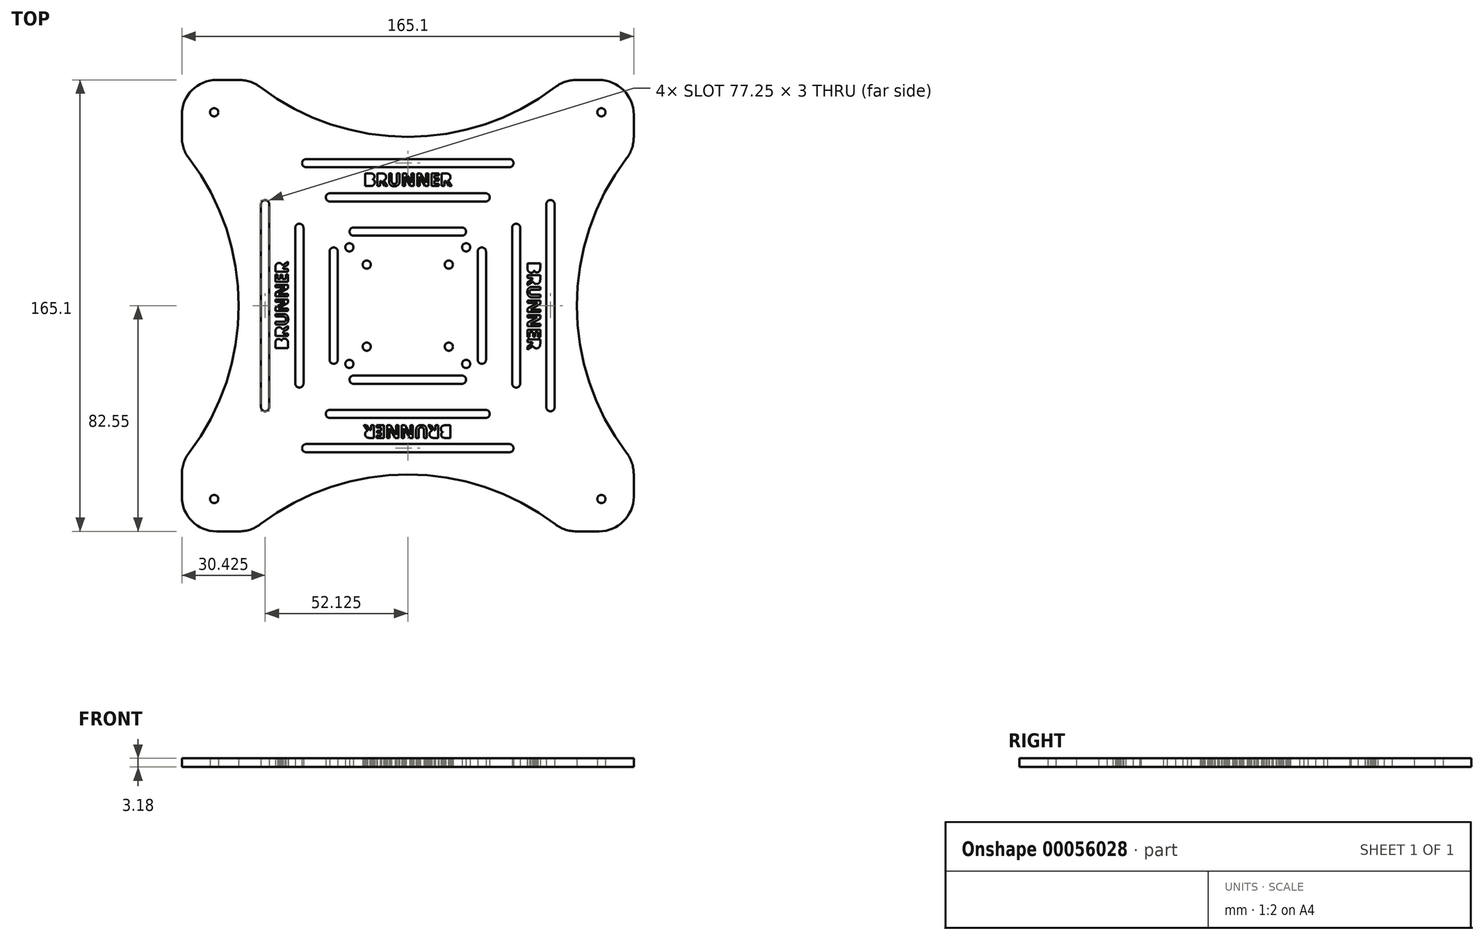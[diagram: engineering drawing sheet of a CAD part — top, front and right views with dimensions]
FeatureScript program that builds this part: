
annotation { "Feature Type Name" : "Feature", "Feature Type Description" : "" }
export const myFeature = defineFeature(function(context is Context, id is Id, definition is map)
    precondition{}
    {
        {
            var Q0;
            Q0=qCreatedBy(makeId("Top.planeOp"),FACE);
            var sketch = newSketch(context, id + "F0", { "sketchPlane" : qUnion([Q0])});
            skLineSegment(sketch, "E0.rect.bottom", {"start": v(-82.55, 82.55) * mm, "end": v(82.55, 82.55) * mm});
            skLineSegment(sketch, "E0.rect.top", {"start": v(-82.55, -82.55) * mm, "end": v(82.55, -82.55) * mm});
            skLineSegment(sketch, "E0.rect.left", {"start": v(-82.55, 82.55) * mm, "end": v(-82.55, -82.55) * mm});
            skLineSegment(sketch, "E0.rect.right", {"start": v(82.55, 82.55) * mm, "end": v(82.55, -82.55) * mm});
            skPoint(sketch, "E0.rect.middle", {"position": v(0, 0) * mm});
            skCircle(sketch, "E1", {"center": v(-70.72, 70.72) * mm, "radius": 1.5 * mm});
            skLineSegment(sketch, "E2", {"start": v(0, 0) * mm, "end": v(-82.55, 82.55) * mm});
            skCircle(sketch, "E3", {"center": v(-15, 15) * mm, "radius": 1.5 * mm});
            skArc(sketch, "E4", {"start": v(-82.55, -57.15) * mm, "mid": v(-61.75, 0) * mm, "end": v(-82.55, 57.15) * mm});
            skArc(sketch, "E5.1.0", {"start": v(-57.15, 82.55) * mm, "mid": v(0, 61.75) * mm, "end": v(57.15, 82.55) * mm});
            skLineSegment(sketch, "E5.anchor1", {"start": v(0, 0) * mm, "end": v(-82.55, -57.15) * mm, "construction": true});
            skLineSegment(sketch, "E5.anchor2", {"start": v(0, 0) * mm, "end": v(-57.15, 82.55) * mm, "construction": true});
            skLineSegment(sketch, "E6", {"start": v(-19.78, 28.58) * mm, "end": v(19.78, 28.58) * mm});
            skLineSegment(sketch, "E7", {"start": v(0, 28.58) * mm, "end": v(0, 82.55) * mm, "construction": true});
            skLineSegment(sketch, "E8.0", {"start": v(-19.78, 25.58) * mm, "end": v(19.78, 25.58) * mm});
            skLineSegment(sketch, "E9.0", {"start": v(-28.45, 38.1) * mm, "end": v(28.45, 38.1) * mm});
            skLineSegment(sketch, "E10.0", {"start": v(-28.45, 41.1) * mm, "end": v(28.45, 41.1) * mm});
            skLineSegment(sketch, "E11.0", {"start": v(-37.13, 50.63) * mm, "end": v(37.13, 50.63) * mm});
            skLineSegment(sketch, "E12.0", {"start": v(-37.13, 53.63) * mm, "end": v(37.13, 53.63) * mm});
            skLineSegment(sketch, "E13", {"start": v(0, 0) * mm, "end": v(57.15, 82.55) * mm, "construction": true});
            skLineSegment(sketch, "E14", {"start": v(-37.13, 53.63) * mm, "end": v(-37.13, 50.63) * mm, "construction": true});
            skLineSegment(sketch, "E15", {"start": v(-28.45, 41.1) * mm, "end": v(-28.45, 38.1) * mm, "construction": true});
            skLineSegment(sketch, "E16", {"start": v(-19.78, 28.58) * mm, "end": v(-19.78, 25.58) * mm, "construction": true});
            skArc(sketch, "E17", {"start": v(-19.78, 28.58) * mm, "mid": v(-21.28, 27.08) * mm, "end": v(-19.78, 25.58) * mm});
            skArc(sketch, "E18", {"start": v(-28.45, 41.1) * mm, "mid": v(-29.95, 39.6) * mm, "end": v(-28.45, 38.1) * mm});
            skArc(sketch, "E19", {"start": v(-37.13, 53.63) * mm, "mid": v(-38.63, 52.13) * mm, "end": v(-37.13, 50.63) * mm});
            skArc(sketch, "E20.MirrorCS", {"start": v(37.13, 53.63) * mm, "mid": v(38.63, 52.13) * mm, "end": v(37.13, 50.63) * mm});
            skArc(sketch, "E21.MirrorCS", {"start": v(28.45, 41.1) * mm, "mid": v(29.95, 39.6) * mm, "end": v(28.45, 38.1) * mm});
            skArc(sketch, "E22.MirrorCS", {"start": v(19.78, 28.58) * mm, "mid": v(21.28, 27.08) * mm, "end": v(19.78, 25.58) * mm});
            skPoint(sketch, "E23.orphan", {"position": v(-57.4, 28.58) * mm});
            skPoint(sketch, "E24.orphan", {"position": v(57.4, 28.58) * mm});
            skCircle(sketch, "E25", {"center": v(-21.33, 21.33) * mm, "radius": 1.5 * mm});
            skLineSegment(sketch, "E26", {"start": v(0, 0) * mm, "end": v(82.55, 82.55) * mm});
            skCircle(sketch, "E27.MirrorC", {"center": v(70.72, 70.72) * mm, "radius": 1.5 * mm});
            skCircle(sketch, "E28.MirrorC", {"center": v(21.33, 21.33) * mm, "radius": 1.5 * mm});
            skCircle(sketch, "E29.MirrorC", {"center": v(15, 15) * mm, "radius": 1.5 * mm});
            skLineSegment(sketch, "E30", {"start": v(-15, 15) * mm, "end": v(15, 15) * mm, "construction": true});
            skText(sketch, "E31", { "text": "BRUNNER", "fontName": "OpenSans-Bold.ttf"});
            const initialGuessF0  = {"E31": [-0.0161, 0.04373, 1, 0, 0.0047]};
            skSetInitialGuess(sketch, initialGuessF0);
            skSolve(sketch);
        }
        {
            var Q0;
            {var subQ10=sQuery(id+"F0.wireOp",EDGE,"E5.1.0");Q0=makeQuery(id+"F0.imprint","IMPRINT",FACE,{"disambiguationData":[TD([[makeQuery(id+"F0.imprint","IMPRINT",EDGE,{"derivedFrom":subQ10}),-1.0]])]});}
            extrude(context, id + "F1", {"entities" : qUnion([Q0]), "depth" : 3.17 * mm});
        }
        {
            var Q0;
            Q0=makeQuery(id+"F1.opExtrude","SWEPT_BODY",BODY,{"disambiguationData":[OSD([sQuery(id+"F0.wireOp",EDGE,"E0.rect.bottom"),sQuery(id+"F0.wireOp",EDGE,"E1"),sQuery(id+"F0.wireOp",EDGE,"E2"),sQuery(id+"F0.wireOp",EDGE,"E3"),sQuery(id+"F0.wireOp",EDGE,"E5.1.0"),sQuery(id+"F0.wireOp",EDGE,"E6"),sQuery(id+"F0.wireOp",EDGE,"E8.0"),sQuery(id+"F0.wireOp",EDGE,"E9.0"),sQuery(id+"F0.wireOp",EDGE,"E10.0"),sQuery(id+"F0.wireOp",EDGE,"E11.0"),sQuery(id+"F0.wireOp",EDGE,"E12.0"),sQuery(id+"F0.wireOp",EDGE,"E17"),sQuery(id+"F0.wireOp",EDGE,"E18"),sQuery(id+"F0.wireOp",EDGE,"E19"),sQuery(id+"F0.wireOp",EDGE,"E20.MirrorCS"),sQuery(id+"F0.wireOp",EDGE,"E21.MirrorCS"),sQuery(id+"F0.wireOp",EDGE,"E22.MirrorCS"),sQuery(id+"F0.wireOp",EDGE,"E25"),sQuery(id+"F0.wireOp",EDGE,"E26")])]});
            var Q1;
            Q1=makeQuery(id+"F1.opExtrude","SWEPT_EDGE",EDGE,{"disambiguationData":[OSD([sQuery(id+"F0.wireOp",EDGE,"E2"),sQuery(id+"F0.wireOp",EDGE,"E26")])]});
            circularPattern(context, id + "F2", {"operationType" : NewBodyOperationType.ADD, "entities" : qUnion([Q0]), "axis" : qUnion([Q1]), "angle" : 90 * degree, "instanceCount" : 4});
        }
        {
            var Q0;
            {var subQ0=sQuery(id+"F0.wireOp",EDGE,"E0.rect.bottom");Q0=makeQuery(id+"F2.boolean.opBoolean","MERGE",EDGE,{"derivedFrom":[makeQuery(id+"F1.opExtrude","SWEPT_EDGE",EDGE,{"disambiguationData":[OSD([subQ0,sQuery(id+"F0.wireOp",EDGE,"E0.rect.left"),sQuery(id+"F0.wireOp",EDGE,"E2")])]}),makeQuery(id+"F2.opPattern","COPY",EDGE,{"derivedFrom":makeQuery(id+"F1.opExtrude","SWEPT_EDGE",EDGE,{"disambiguationData":[OSD([subQ0,sQuery(id+"F0.wireOp",EDGE,"E0.rect.right"),sQuery(id+"F0.wireOp",EDGE,"E26")])]}),"instanceName":"3"})]});}
            var Q1;
            {var subQ0=sQuery(id+"F0.wireOp",EDGE,"E0.rect.bottom");Q1=makeQuery(id+"F2.boolean.opBoolean","MERGE",EDGE,{"derivedFrom":[makeQuery(id+"F1.opExtrude","SWEPT_EDGE",EDGE,{"disambiguationData":[OSD([subQ0,sQuery(id+"F0.wireOp",EDGE,"E0.rect.right"),sQuery(id+"F0.wireOp",EDGE,"E26")])]}),makeQuery(id+"F2.opPattern","COPY",EDGE,{"derivedFrom":makeQuery(id+"F1.opExtrude","SWEPT_EDGE",EDGE,{"disambiguationData":[OSD([subQ0,sQuery(id+"F0.wireOp",EDGE,"E0.rect.left"),sQuery(id+"F0.wireOp",EDGE,"E2")])]}),"instanceName":"1"})]});}
            var Q2;
            {var subQ0=sQuery(id+"F0.wireOp",EDGE,"E0.rect.bottom");Q2=makeQuery(id+"F2.boolean.opBoolean","MERGE",EDGE,{"derivedFrom":[makeQuery(id+"F2.opPattern","COPY",EDGE,{"derivedFrom":makeQuery(id+"F1.opExtrude","SWEPT_EDGE",EDGE,{"disambiguationData":[OSD([subQ0,sQuery(id+"F0.wireOp",EDGE,"E0.rect.right"),sQuery(id+"F0.wireOp",EDGE,"E26")])]}),"instanceName":"1"}),makeQuery(id+"F2.opPattern","COPY",EDGE,{"derivedFrom":makeQuery(id+"F1.opExtrude","SWEPT_EDGE",EDGE,{"disambiguationData":[OSD([subQ0,sQuery(id+"F0.wireOp",EDGE,"E0.rect.left"),sQuery(id+"F0.wireOp",EDGE,"E2")])]}),"instanceName":"2"})]});}
            var Q3;
            {var subQ0=sQuery(id+"F0.wireOp",EDGE,"E0.rect.bottom");Q3=makeQuery(id+"F2.boolean.opBoolean","MERGE",EDGE,{"derivedFrom":[makeQuery(id+"F2.opPattern","COPY",EDGE,{"derivedFrom":makeQuery(id+"F1.opExtrude","SWEPT_EDGE",EDGE,{"disambiguationData":[OSD([subQ0,sQuery(id+"F0.wireOp",EDGE,"E0.rect.right"),sQuery(id+"F0.wireOp",EDGE,"E26")])]}),"instanceName":"2"}),makeQuery(id+"F2.opPattern","COPY",EDGE,{"derivedFrom":makeQuery(id+"F1.opExtrude","SWEPT_EDGE",EDGE,{"disambiguationData":[OSD([subQ0,sQuery(id+"F0.wireOp",EDGE,"E0.rect.left"),sQuery(id+"F0.wireOp",EDGE,"E2")])]}),"instanceName":"3"})]});}
            var Q4;
            {var subQ0=sQuery(id+"F0.wireOp",EDGE,"E5.1.0");var subQ1=sQuery(id+"F0.wireOp",EDGE,"E0.rect.bottom");Q4=makeQuery(id+"F2.opPattern","COPY",EDGE,{"derivedFrom":makeQuery(id+"F1.opExtrude","SWEPT_EDGE",EDGE,{"disambiguationData":[OSD([subQ1,subQ0]),TDD([makeQuery(id+"F0.imprint","INTERSECT",VERTEX,{"disambiguationData":[OD(1.0)],"derivedFrom":[subQ1,subQ0]})])]}),"instanceName":"2"});}
            var Q5;
            {var subQ0=sQuery(id+"F0.wireOp",EDGE,"E5.1.0");var subQ1=sQuery(id+"F0.wireOp",EDGE,"E0.rect.bottom");Q5=makeQuery(id+"F2.opPattern","COPY",EDGE,{"derivedFrom":makeQuery(id+"F1.opExtrude","SWEPT_EDGE",EDGE,{"disambiguationData":[OSD([subQ1,subQ0]),TDD([makeQuery(id+"F0.imprint","INTERSECT",VERTEX,{"disambiguationData":[OD(0.0)],"derivedFrom":[subQ1,subQ0]})])]}),"instanceName":"2"});}
            var Q6;
            {var subQ0=sQuery(id+"F0.wireOp",EDGE,"E5.1.0");var subQ1=sQuery(id+"F0.wireOp",EDGE,"E0.rect.bottom");Q6=makeQuery(id+"F2.opPattern","COPY",EDGE,{"derivedFrom":makeQuery(id+"F1.opExtrude","SWEPT_EDGE",EDGE,{"disambiguationData":[OSD([subQ1,subQ0]),TDD([makeQuery(id+"F0.imprint","INTERSECT",VERTEX,{"disambiguationData":[OD(0.0)],"derivedFrom":[subQ1,subQ0]})])]}),"instanceName":"3"});}
            var Q7;
            {var subQ0=sQuery(id+"F0.wireOp",EDGE,"E5.1.0");var subQ1=sQuery(id+"F0.wireOp",EDGE,"E0.rect.bottom");Q7=makeQuery(id+"F2.opPattern","COPY",EDGE,{"derivedFrom":makeQuery(id+"F1.opExtrude","SWEPT_EDGE",EDGE,{"disambiguationData":[OSD([subQ1,subQ0]),TDD([makeQuery(id+"F0.imprint","INTERSECT",VERTEX,{"disambiguationData":[OD(1.0)],"derivedFrom":[subQ1,subQ0]})])]}),"instanceName":"3"});}
            var Q8;
            {var subQ0=sQuery(id+"F0.wireOp",EDGE,"E5.1.0");var subQ1=sQuery(id+"F0.wireOp",EDGE,"E0.rect.bottom");Q8=makeQuery(id+"F1.opExtrude","SWEPT_EDGE",EDGE,{"disambiguationData":[OSD([subQ1,subQ0]),TDD([makeQuery(id+"F0.imprint","INTERSECT",VERTEX,{"disambiguationData":[OD(0.0)],"derivedFrom":[subQ1,subQ0]})])]});}
            var Q9;
            {var subQ0=sQuery(id+"F0.wireOp",EDGE,"E5.1.0");var subQ1=sQuery(id+"F0.wireOp",EDGE,"E0.rect.bottom");Q9=makeQuery(id+"F1.opExtrude","SWEPT_EDGE",EDGE,{"disambiguationData":[OSD([subQ1,subQ0]),TDD([makeQuery(id+"F0.imprint","INTERSECT",VERTEX,{"disambiguationData":[OD(1.0)],"derivedFrom":[subQ1,subQ0]})])]});}
            var Q10;
            {var subQ0=sQuery(id+"F0.wireOp",EDGE,"E5.1.0");var subQ1=sQuery(id+"F0.wireOp",EDGE,"E0.rect.bottom");Q10=makeQuery(id+"F2.opPattern","COPY",EDGE,{"derivedFrom":makeQuery(id+"F1.opExtrude","SWEPT_EDGE",EDGE,{"disambiguationData":[OSD([subQ1,subQ0]),TDD([makeQuery(id+"F0.imprint","INTERSECT",VERTEX,{"disambiguationData":[OD(1.0)],"derivedFrom":[subQ1,subQ0]})])]}),"instanceName":"1"});}
            var Q11;
            {var subQ0=sQuery(id+"F0.wireOp",EDGE,"E5.1.0");var subQ1=sQuery(id+"F0.wireOp",EDGE,"E0.rect.bottom");Q11=makeQuery(id+"F2.opPattern","COPY",EDGE,{"derivedFrom":makeQuery(id+"F1.opExtrude","SWEPT_EDGE",EDGE,{"disambiguationData":[OSD([subQ1,subQ0]),TDD([makeQuery(id+"F0.imprint","INTERSECT",VERTEX,{"disambiguationData":[OD(0.0)],"derivedFrom":[subQ1,subQ0]})])]}),"instanceName":"1"});}
            fillet(context, id + "F3", {"entities" : qUnion([Q0, Q1, Q2, Q3, Q4, Q5, Q6, Q7, Q8, Q9, Q10, Q11]), "radius" : 12.7 * mm, "tangentPropagation" : true, "allowEdgeOverflow" : false});
        }
    });
